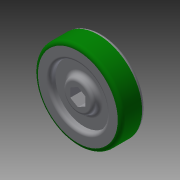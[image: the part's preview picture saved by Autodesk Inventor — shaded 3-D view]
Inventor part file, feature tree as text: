
AUTODESK INVENTOR PART (.ipt)
format: ipt  version: 2015 (Build 190159000, 159)  size: 248,832 bytes
history: native  units: in
note: dims shown in document units (in); Inventor stores cm internally (conversion verified against a paired STEP export)
features: extrude x4, fillet x4, mirror x4, sketch x3, plane x1
ambient origin geometry x8: Origin, YZ Plane, XZ Plane, XY Plane, X Axis, Y Axis, Z Axis, Center Point
bodies: Solid1 (feature_tree)
feature tree (16):
  sketch  "Sketch1"  dims[d0=2.875in d1=1.875in]
  extrude  "Extrusion1"  Depth=1.875in
  extrude  "Extrusion2"  Depth=0.8in TaperAngle=0.0deg
  fillet  "Fillet1"  Radius=0.125in
  fillet  "Fillet2"  Radius=0.1in
  extrude  "Extrusion3"  Depth=0.5in TaperAngle=0.0deg
  fillet  "Fillet3"  Radius=0.125in
  fillet  "Fillet4"  Radius=0.1in
  plane  "Work Plane2"
  mirror  "Mirror1"
  mirror  "Mirror2"
  mirror  "Mirror3"
  mirror  "Mirror4"
  extrude  "Extrusion4"  Depth=0.5in
  sketch  "Sketch2"  dims[d2=0.8in d3=0.0in d4=0.2in d5=0.0in d6=0.125in d7=0.1in]
  sketch  "Sketch3"  dims[d8=1.0in d9=0.2in d10=0.0in d11=0.125in d12=0.1in d13=0.5in d14=10.0in d15=0.0in d35=-0.4in]
